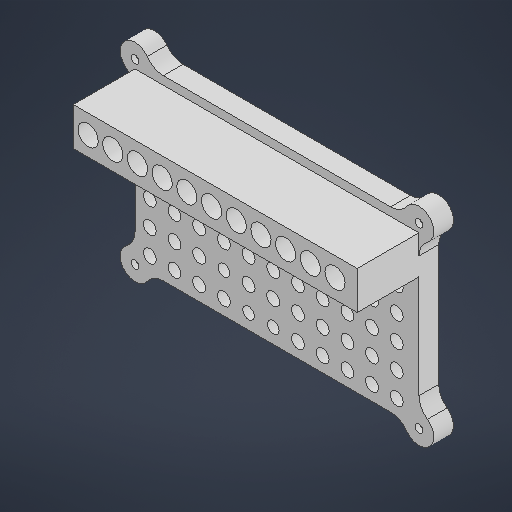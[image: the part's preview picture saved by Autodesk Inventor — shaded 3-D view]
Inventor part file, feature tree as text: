
AUTODESK INVENTOR PART (.ipt)
format: ipt  version: 2025.1 (Build 291241000, 241)  size: 1,130,496 bytes
history: native  units: in
note: dims shown in document units (in); Inventor stores cm internally (conversion verified against a paired STEP export)
features: sketch x12, extrude x8, projected_geometry x3, fillet x1
ambient origin geometry x8: Origin, YZ Plane, XZ Plane, XY Plane, X Axis, Y Axis, Z Axis, Center Point
bodies: Solid1 (feature_tree)
feature tree (24):
  extrude  "Extrusion1"  Depth=2.8346in
  extrude  "Extrusion2"  Depth=0.2362in
  extrude  "Extrusion3"  Depth=0.3937in
  extrude  "Extrusion4"  Depth=0.2362in
  fillet  "Fillet1"  Radius=0.4724in
  extrude  "Extrusion5"  Depth=0.4724in
  extrude  "Extrusion6"  Depth=0.315in TaperAngle=0.0deg
  extrude  "Extrusion7"  Depth=0.315in
  extrude  "Extrusion8"  Depth=0.315in
  sketch  "Sketch1"  dims[d0=4.5276in d1=2.8346in]
  sketch  "Sketch Rectangular Pattern1"  dims[d2=0.185in d3=0.2362in]
  sketch  "Sketch2"  dims[d4=0.2362in d5=2.7559in d7=0.3937in d8=4.3307in d10=0.3937in]
  projected_geometry  "Projected Loop1"
  sketch  "Sketch3"  dims[d16=0.4724in d17=0.4724in]
  sketch  "Sketch4"  dims[d21=0.315in d22=0.315in]
  sketch  "Sketch Rectangular Pattern2"  dims[d13=0.2362in d14=0.2362in d15=0.4724in]
  sketch  "Sketch5"  dims[d25=0.315in d26=0.0in]
  projected_geometry  "Projected Loop2"
  sketch  "Sketch Rectangular Pattern3"  dims[d18=0.4724in d19=0.315in d20=0.0in]
  sketch  "Sketch7"  dims[d27=0.0787in d28=0.0in]
  sketch  "Sketch8"  dims[d29=0.126in]
  sketch  "Sketch Rectangular Pattern4"  dims[d23=0.315in d24=0.315in]
  sketch  "Sketch9"  dims[d30=0.126in d31=0.126in d32=0.126in d33=0.8912in d34=0.0in d35=0.315in d36=0.185in d37=0.2047in d38=4.3307in d40=0.3937in d41=2.7559in d43=0.3937in d46=0.2067in d47=2.7559in d49=0.3937in d50=4.3307in d52=0.3937in d55=0.3937in d56=0.0in d57=0.9843in d58=0.0in d59=0.3228in d60=0.2362in d61=4.3307in d63=0.3937in d64=0.3937in d66=0.3937in d68=1.6093in d69=0.0in d70=1.6093in d71=0.0in d73=0.0in d74=0.0in d75=0.0in d76=0.0in]
  projected_geometry  "Projected Loop3"
